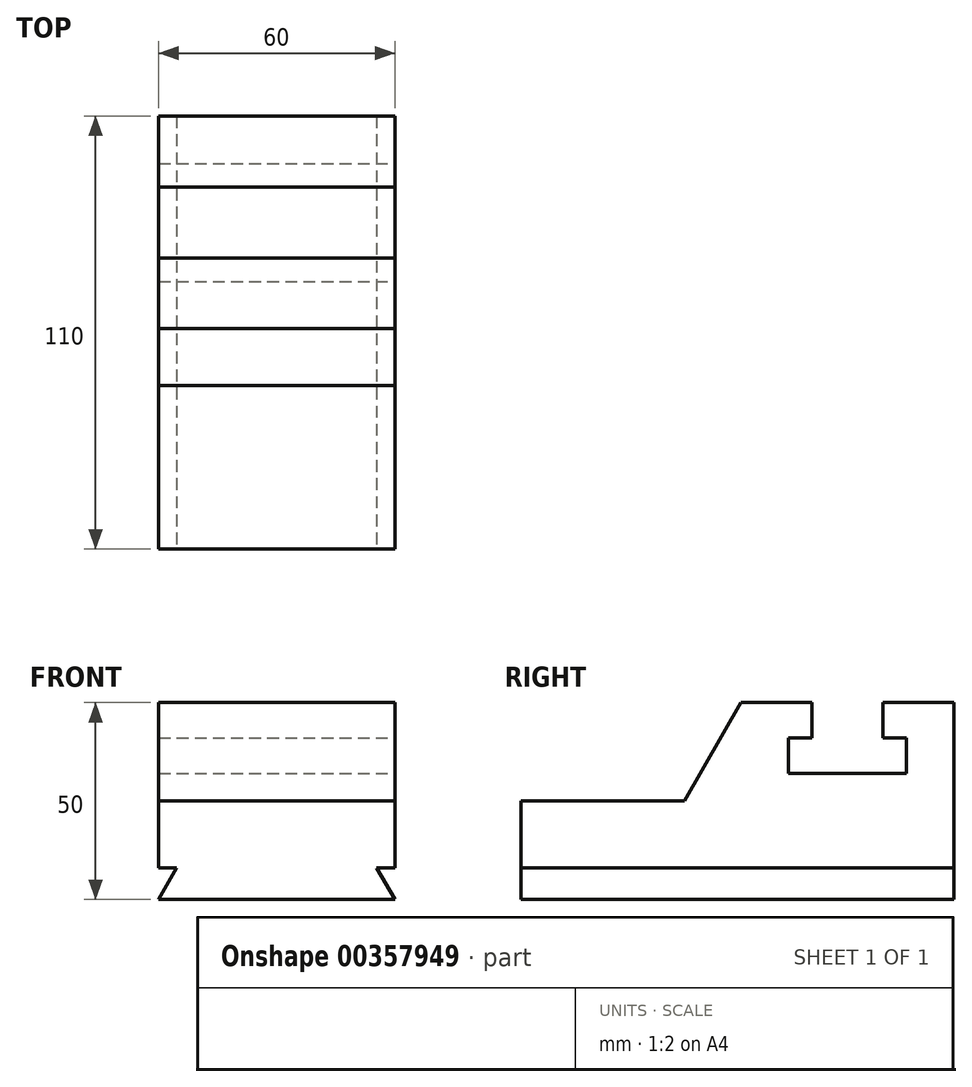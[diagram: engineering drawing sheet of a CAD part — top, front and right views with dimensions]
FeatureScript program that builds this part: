
annotation { "Feature Type Name" : "Feature", "Feature Type Description" : "" }
export const myFeature = defineFeature(function(context is Context, id is Id, definition is map)
    precondition{}
    {
        {
            var Q0;
            Q0=qCreatedBy(makeId("Top.planeOp"),FACE);
            var sketch = newSketch(context, id + "F0", { "sketchPlane" : qUnion([Q0])});
            skLineSegment(sketch, "E0.bottom", {"start": v(-30, 55) * mm, "end": v(30, 55) * mm});
            skLineSegment(sketch, "E0.top", {"start": v(-30, -55) * mm, "end": v(30, -55) * mm});
            skLineSegment(sketch, "E0.left", {"start": v(-30, 55) * mm, "end": v(-30, -55) * mm});
            skLineSegment(sketch, "E0.right", {"start": v(30, 55) * mm, "end": v(30, -55) * mm});
            skPoint(sketch, "E0.middle", {"position": v(0, 0) * mm});
            skSolve(sketch);
        }
        {
            var Q0;
            Q0 = qSketchRegion(id + "F0", true);
            extrude(context, id + "F1", {"entities" : qUnion([Q0]), "depth" : 50 * mm});
        }
        {
            var Q0;
            Q0=makeQuery(id+"F1.opExtrude","SWEPT_FACE",FACE,{"disambiguationData":[OSD([sQuery(id+"F0.wireOp",EDGE,"E0.right")])]});
            var sketch = newSketch(context, id + "F2", { "sketchPlane" : qUnion([Q0])});
            skLineSegment(sketch, "E1", {"start": v(-55, 25) * mm, "end": v(-13.43, 25) * mm});
            skLineSegment(sketch, "E2", {"start": v(-13.43, 25) * mm, "end": v(1, 50) * mm});
            skLineSegment(sketch, "E3", {"start": v(1, 50) * mm, "end": v(-55, 50) * mm});
            skLineSegment(sketch, "E4", {"start": v(-55, 50) * mm, "end": v(-55, 25) * mm});
            skLineSegment(sketch, "E5", {"start": v(19, 50) * mm, "end": v(19, 41) * mm});
            skLineSegment(sketch, "E6", {"start": v(19, 41) * mm, "end": v(13, 41) * mm});
            skLineSegment(sketch, "E7", {"start": v(13, 41) * mm, "end": v(13, 32) * mm});
            skLineSegment(sketch, "E8", {"start": v(13, 32) * mm, "end": v(43, 32) * mm});
            skLineSegment(sketch, "E9", {"start": v(43, 32) * mm, "end": v(43, 41) * mm});
            skLineSegment(sketch, "E10", {"start": v(43, 41) * mm, "end": v(37, 41) * mm});
            skLineSegment(sketch, "E11", {"start": v(37, 41) * mm, "end": v(37, 50) * mm});
            skLineSegment(sketch, "E12", {"start": v(37, 50) * mm, "end": v(19, 50) * mm});
            skSolve(sketch);
        }
        {
            var Q0;
            Q0 = qSketchRegion(id + "F2", true);
            extrude(context, id + "F3", {"entities" : qUnion([Q0]), "operationType" : NewBodyOperationType.REMOVE, "endBound" : BoundingType.THROUGH_ALL, "oppositeDirection" : true, "depth" : 25 * mm});
        }
        {
            var Q0;
            Q0=makeQuery(id+"F1.opExtrude","SWEPT_FACE",FACE,{"disambiguationData":[OSD([sQuery(id+"F0.wireOp",EDGE,"E0.top")])]});
            var sketch = newSketch(context, id + "F4", { "sketchPlane" : qUnion([Q0])});
            skLineSegment(sketch, "E13", {"start": v(30, 0) * mm, "end": v(25.38, 8) * mm});
            skLineSegment(sketch, "E14", {"start": v(25.38, 8) * mm, "end": v(30, 8) * mm});
            skLineSegment(sketch, "E15", {"start": v(30, 8) * mm, "end": v(30, 0) * mm});
            skLineSegment(sketch, "E16", {"start": v(-30, 8) * mm, "end": v(-30, 0) * mm});
            skLineSegment(sketch, "E17", {"start": v(-30, 8) * mm, "end": v(-25.38, 8) * mm});
            skLineSegment(sketch, "E18", {"start": v(-25.38, 8) * mm, "end": v(-30, 0) * mm});
            skSolve(sketch);
        }
        {
            var Q0;
            Q0 = qSketchRegion(id + "F4", true);
            extrude(context, id + "F5", {"entities" : qUnion([Q0]), "operationType" : NewBodyOperationType.REMOVE, "endBound" : BoundingType.THROUGH_ALL, "oppositeDirection" : true, "depth" : 25 * mm});
        }
    });
